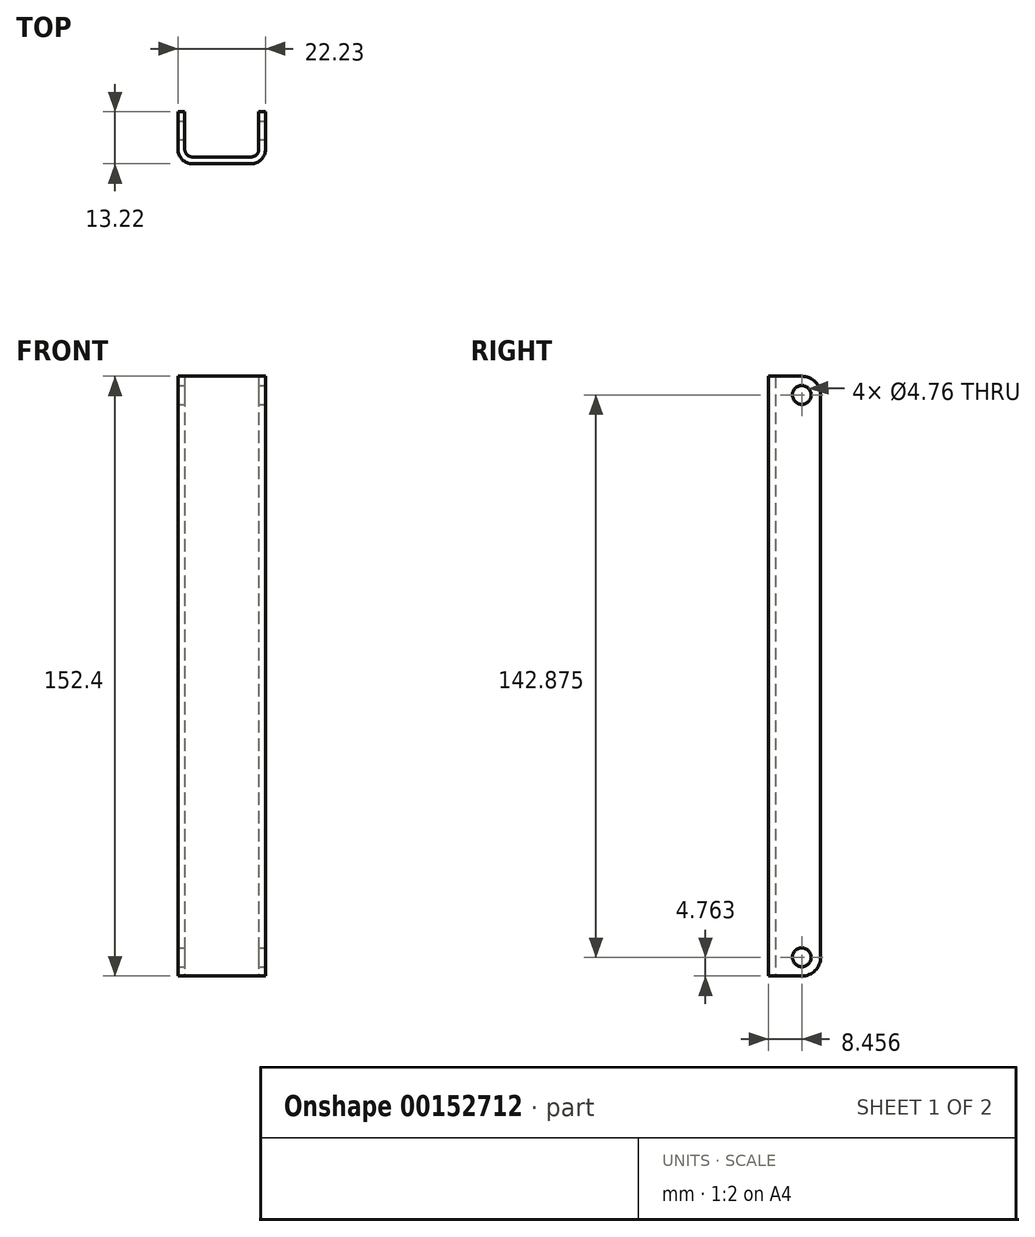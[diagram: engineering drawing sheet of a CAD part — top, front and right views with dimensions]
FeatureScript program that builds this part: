
annotation { "Feature Type Name" : "Feature", "Feature Type Description" : "" }
export const myFeature = defineFeature(function(context is Context, id is Id, definition is map)
    precondition{}
    {
        {
            var Q0;
            Q0=qCreatedBy(makeId("Top.planeOp"),FACE);
            var sketch = newSketch(context, id + "F0", { "sketchPlane" : qUnion([Q0])});
            skLineSegment(sketch, "E0.bottom", {"start": v(0, 0) * mm, "end": v(-18.8, 0) * mm});
            skLineSegment(sketch, "E0.top", {"start": v(1.7, -1.7) * mm, "end": v(-20.52, -1.7) * mm});
            skLineSegment(sketch, "E1.top", {"start": v(-18.8, 11.5) * mm, "end": v(-20.52, 11.5) * mm});
            skLineSegment(sketch, "E1.left", {"start": v(-18.8, 0) * mm, "end": v(-18.8, 11.5) * mm});
            skLineSegment(sketch, "E1.right", {"start": v(-20.52, -1.7) * mm, "end": v(-20.52, 11.5) * mm});
            skLineSegment(sketch, "E2.top", {"start": v(0, 11.5) * mm, "end": v(1.7, 11.5) * mm});
            skLineSegment(sketch, "E2.left", {"start": v(0, 0) * mm, "end": v(0, 11.5) * mm});
            skLineSegment(sketch, "E2.right", {"start": v(1.7, -1.7) * mm, "end": v(1.7, 11.5) * mm});
            skLineSegment(sketch, "E3", {"start": v(-9.4, 0) * mm, "end": v(-9.4, -1.7) * mm, "construction": true});
            skLineSegment(sketch, "E4", {"start": v(-18.8, 0) * mm, "end": v(-20.52, -1.7) * mm, "construction": true});
            skSolve(sketch);
        }
        {
            var Q0;
            Q0=qSketchRegion(id+"F0",true);
            extrude(context, id + "F1", {"entities" : qUnion([Q0]), "depth" : 152.4 * mm});
        }
        {
            var Q0;
            Q0=makeQuery(id+"FcdIcV9w6YY9zah_1.opExtrude","CAP_EDGE",EDGE,{"disambiguationData":[OSD([sQuery(id+"FU7sgaIbCbRhSfr_1.wireOp",EDGE,"F29Sxc5V-O2cl-wjtz-gx5o-reTTBG7m1pNU.top")])],"isStart":true});
            var Q1;
            Q1=makeQuery(id+"FcdIcV9w6YY9zah_1.opExtrude","CAP_EDGE",EDGE,{"disambiguationData":[OSD([sQuery(id+"FU7sgaIbCbRhSfr_1.wireOp",EDGE,"yv2bQU74-Eht6-uYuo-WBF2-3C4kyuaz0slr.top")])],"isStart":true});
            var Q2;
            Q2=makeQuery(id+"F1.opExtrude","SWEPT_EDGE",EDGE,{"disambiguationData":[OSD([sQuery(id+"F0.wireOp",EDGE,"E0.bottom"),sQuery(id+"F0.wireOp",EDGE,"E2.left")])]});
            var Q3;
            Q3=makeQuery(id+"F1.opExtrude","SWEPT_EDGE",EDGE,{"disambiguationData":[OSD([sQuery(id+"F0.wireOp",EDGE,"E0.bottom"),sQuery(id+"F0.wireOp",EDGE,"E1.left")])]});
            fillet(context, id + "F2", {"entities" : qUnion([Q0, Q1, Q2, Q3]), "radius" : 1.98 * mm, "tangentPropagation" : true, "allowEdgeOverflow" : false});
        }
        {
            var Q0;
            Q0=makeQuery(id+"F1.opExtrude","SWEPT_EDGE",EDGE,{"disambiguationData":[OSD([sQuery(id+"F0.wireOp",EDGE,"E0.top"),sQuery(id+"F0.wireOp",EDGE,"E2.right")])]});
            var Q1;
            Q1=makeQuery(id+"F1.opExtrude","SWEPT_EDGE",EDGE,{"disambiguationData":[OSD([sQuery(id+"F0.wireOp",EDGE,"E0.top"),sQuery(id+"F0.wireOp",EDGE,"E1.right")])]});
            fillet(context, id + "F3", {"entities" : qUnion([Q0, Q1]), "radius" : 3.7 * mm, "tangentPropagation" : true, "allowEdgeOverflow" : false});
        }
        {
            var Q0;
            Q0=makeQuery(id+"F1.opExtrude","CAP_EDGE",EDGE,{"disambiguationData":[OSD([sQuery(id+"F0.wireOp",EDGE,"E2.top")])],"isStart":false});
            var Q1;
            Q1=makeQuery(id+"F1.opExtrude","CAP_EDGE",EDGE,{"disambiguationData":[OSD([sQuery(id+"F0.wireOp",EDGE,"E1.top")])],"isStart":false});
            var Q2;
            Q2=makeQuery(id+"F1.opExtrude","CAP_EDGE",EDGE,{"disambiguationData":[OSD([sQuery(id+"F0.wireOp",EDGE,"E1.top")])],"isStart":true});
            var Q3;
            Q3=makeQuery(id+"F1.opExtrude","CAP_EDGE",EDGE,{"disambiguationData":[OSD([sQuery(id+"F0.wireOp",EDGE,"E2.top")])],"isStart":true});
            fillet(context, id + "F4", {"entities" : qUnion([Q0, Q1, Q2, Q3]), "radius" : 4.76 * mm, "tangentPropagation" : true, "allowEdgeOverflow" : false});
        }
        {
            var Q0;
            Q0=makeQuery(id+"F1.opExtrude","SWEPT_FACE",FACE,{"disambiguationData":[OSD([sQuery(id+"F0.wireOp",EDGE,"E2.right")])]});
            var sketch = newSketch(context, id + "F5", { "sketchPlane" : qUnion([Q0])});
            skCircle(sketch, "E5", {"center": v(6.75, 4.76) * mm, "radius": 2.38 * mm});
            skCircle(sketch, "E6", {"center": v(6.75, 147.64) * mm, "radius": 2.38 * mm});
            skSolve(sketch);
        }
        {
            var Q0;
            Q0 = qSketchRegion(id + "F5", true);
            var Q1;
            Q1=makeQuery(id+"F1.opExtrude","SWEPT_FACE",FACE,{"disambiguationData":[OSD([sQuery(id+"F0.wireOp",EDGE,"E1.right")])]});
            extrude(context, id + "F6", {"entities" : qUnion([Q0]), "operationType" : NewBodyOperationType.REMOVE, "endBound" : BoundingType.UP_TO_SURFACE, "oppositeDirection" : true, "endBoundEntityFace" : qUnion([Q1]), "depth" : 25.4 * mm});
        }
    });
